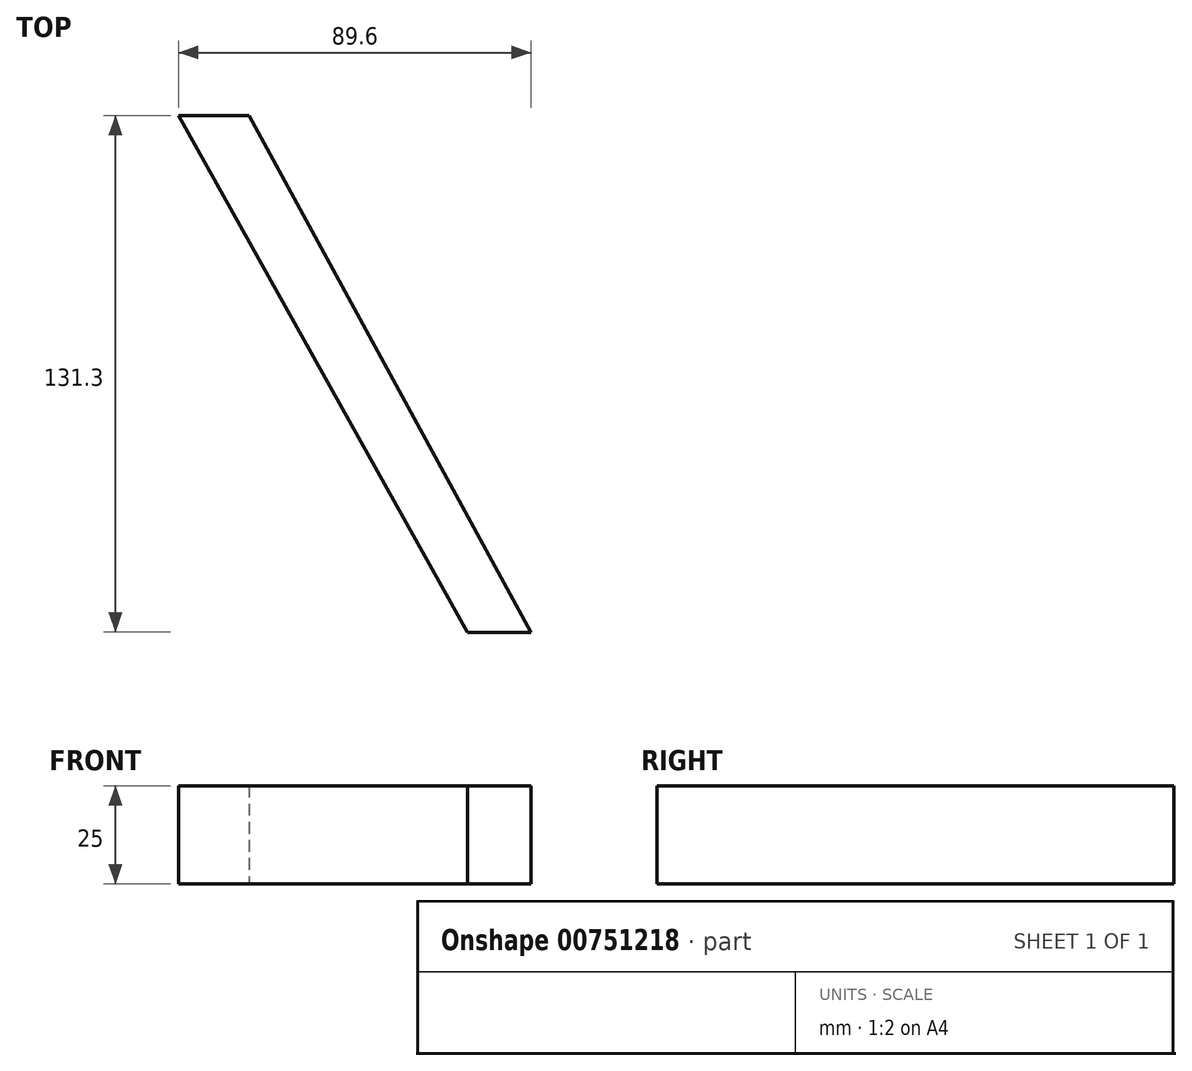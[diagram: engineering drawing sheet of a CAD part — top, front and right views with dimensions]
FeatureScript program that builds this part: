
annotation { "Feature Type Name" : "Feature", "Feature Type Description" : "" }
export const myFeature = defineFeature(function(context is Context, id is Id, definition is map)
    precondition{}
    {
        {
            var Q0;
            Q0=qCreatedBy(makeId("Top.planeOp"),FACE);
            var sketch = newSketch(context, id + "F0", { "sketchPlane" : qUnion([Q0])});
            skLineSegment(sketch, "E0", {"start": v(40.4, 0) * mm, "end": v(86.08, -89.21) * mm});
            skLineSegment(sketch, "E1", {"start": v(86.08, -89.21) * mm, "end": v(40.4, -89.21) * mm});
            skLineSegment(sketch, "E2", {"start": v(40.4, -89.21) * mm, "end": v(-33.02, 42.09) * mm});
            skLineSegment(sketch, "E3", {"start": v(-33.02, 42.09) * mm, "end": v(-15, 42.09) * mm});
            skLineSegment(sketch, "E4", {"start": v(-15, 42.09) * mm, "end": v(56.58, -89.21) * mm});
            skSolve(sketch);
        }
        {
            var Q0;
            {var subQ0=sQuery(id+"F0.wireOp",EDGE,"E2");Q0=makeQuery(id+"F0.imprint","IMPRINT",FACE,{"disambiguationData":[TD([[makeQuery(id+"F0.imprint","IMPRINT",EDGE,{"derivedFrom":subQ0}),-1.0]])]});}
            extrude(context, id + "F1", {"entities" : qUnion([Q0]), "depth" : 25 * mm, "offsetDistance" : 25 * mm});
        }
    });
